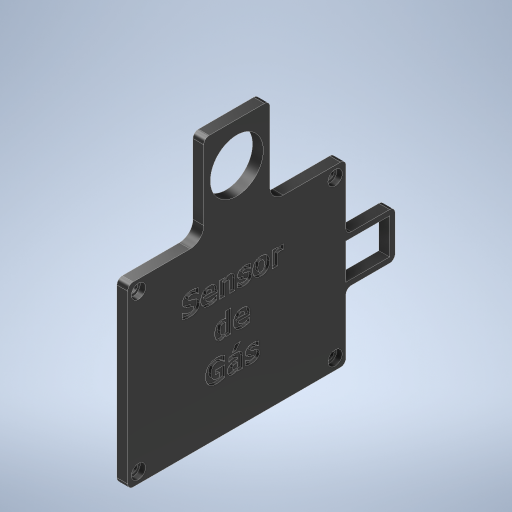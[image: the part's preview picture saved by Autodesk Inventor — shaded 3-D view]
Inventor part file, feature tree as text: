
AUTODESK INVENTOR PART (.ipt)
format: ipt  version: 2023 (Build 270158000, 158)  size: 664,064 bytes
history: native  units: mm
features: extrude x6, sketch x6, fillet x2, other x1
ambient origin geometry x8: Origin, YZ Plane, XZ Plane, XY Plane, X Axis, Y Axis, Z Axis, Center Point
bodies: Body1 (feature_tree)
feature tree (15):
  other  "Sólido1"
  extrude  "Extrusão1"  Depth=65.8mm
  extrude  "Extrusão2"  Depth=65.8mm
  extrude  "Extrusão3"  Depth=32.9mm
  extrude  "Extrusão4"  Depth=2.0mm
  fillet  "Arredondamento1"  Radius=4.0mm
  extrude  "Extrusão5"  Depth=3.2mm
  fillet  "Arredondamento2"  Radius=3.2mm
  extrude  "Extrusão6"  Depth=4.0mm
  sketch  "Esboço1"  dims[d0=80.8mm d1=65.8mm]
  sketch  "Esboço2"  dims[d2=28.15mm d3=65.8mm]
  sketch  "Esboço3"  dims[d4=28.15mm d5=32.9mm]
  sketch  "Esboço4"  dims[d6=32.9mm d7=2.0mm d8=4.0mm d9=0.0mm]
  sketch  "Esboço5"  dims[d10=3.2mm d11=3.2mm d12=3.2mm]
  sketch  "Esboço6"  dims[d13=3.2mm d14=4.0mm d15=4.0mm d16=4.0mm d17=4.0mm d18=4.0mm d19=4.0mm d20=4.0mm d21=4.0mm d22=19.6mm d23=14.8mm d24=24.5mm d25=12.25mm d26=2.0mm d27=0.0mm d28=5.2mm d29=5.3mm d30=5.2mm d31=5.2mm d32=2.0mm d33=0.0mm d34=1.0mm d35=0.0mm d36=5.0mm d37=18.2mm d38=17.2mm d39=65.8mm d40=24.3mm d41=4.0mm d42=0.0mm d43=2.0mm d44=16.2mm d45=13.2mm d46=2.0mm d47=2.0mm d48=4.0mm d49=0.0mm]
